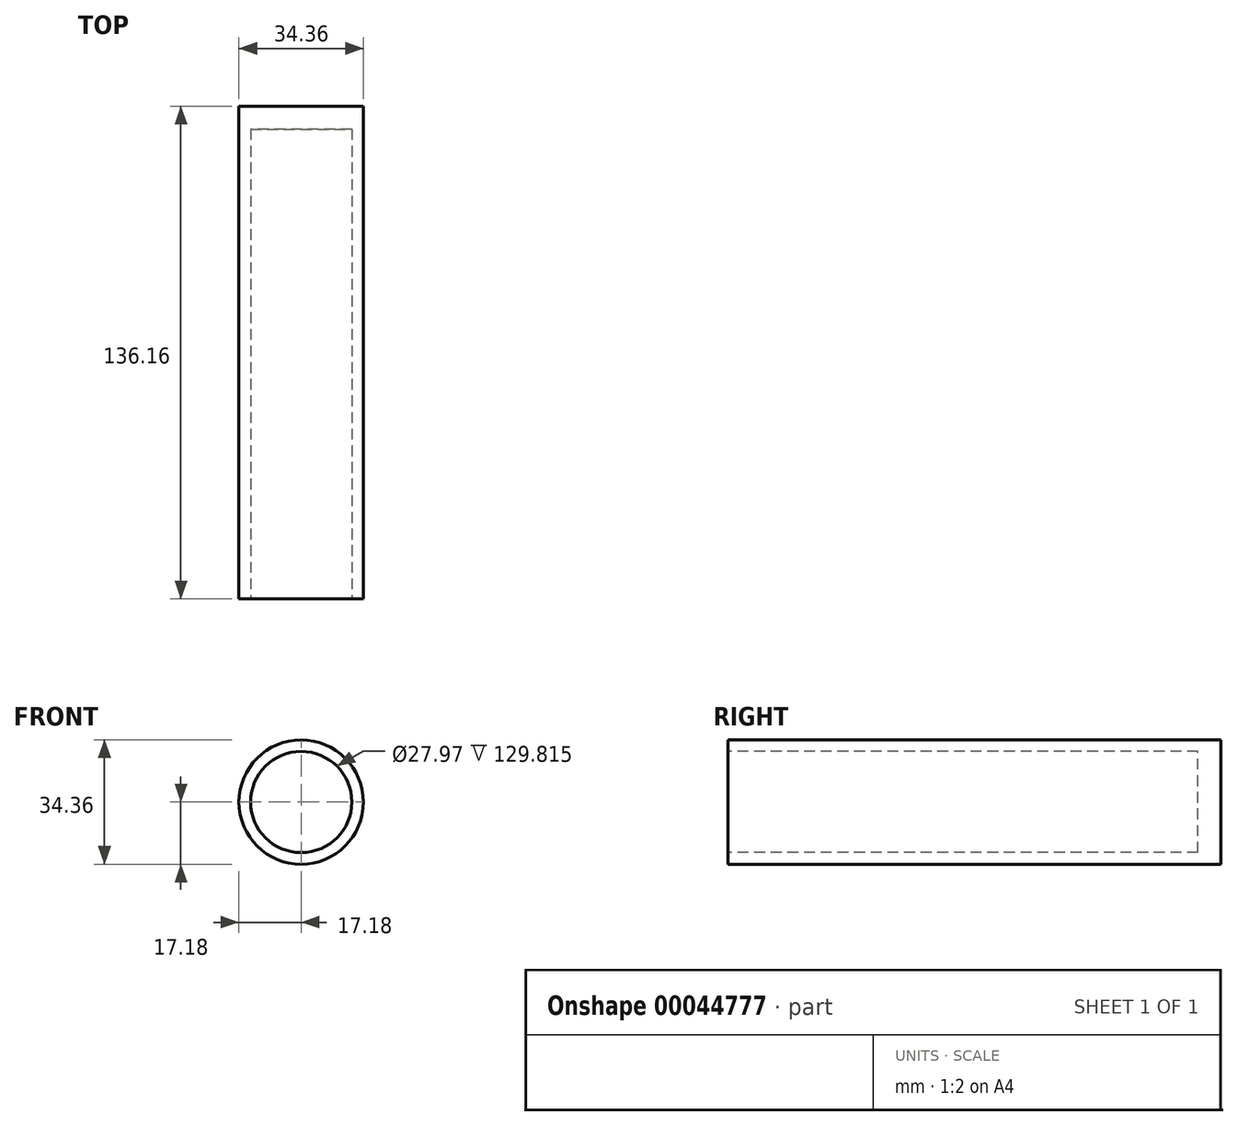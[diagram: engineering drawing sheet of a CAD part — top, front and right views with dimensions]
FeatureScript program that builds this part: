
annotation { "Feature Type Name" : "Feature", "Feature Type Description" : "" }
export const myFeature = defineFeature(function(context is Context, id is Id, definition is map)
    precondition{}
    {
        {
            var Q0;
            Q0=qCreatedBy(makeId("Front.planeOp"),FACE);
            var sketch = newSketch(context, id + "F0", { "sketchPlane" : qUnion([Q0])});
            skCircle(sketch, "E0", {"center": v(0, 0) * mm, "radius": 17.18 * mm});
            skSolve(sketch);
        }
        {
            var Q0;
            Q0=makeQuery(id+"F0.imprint","IMPRINT",FACE,{"disambiguationData":[TD([[makeQuery(id+"F0.imprint","IMPRINT",EDGE,{"derivedFrom":sQuery(id+"F0.wireOp",EDGE,"E0")}),1.0]])]});
            cPlane(context, id + "F1", {"entities" : qUnion([Q0]), "cplaneType" : CPlaneType.OFFSET, "offset" : 6.35 * mm, "width" : 152.4 * mm, "height" : 152.4 * mm});
        }
        {
            var Q0;
            Q0=makeQuery(id+"F0.imprint","IMPRINT",FACE,{"disambiguationData":[TD([[makeQuery(id+"F0.imprint","IMPRINT",EDGE,{"derivedFrom":sQuery(id+"F0.wireOp",EDGE,"E0")}),1.0]])]});
            extrude(context, id + "F2", {"entities" : qUnion([Q0]), "depth" : 136.16 * mm});
        }
        {
            var Q0;
            Q0=makeQuery(id+"F2.opExtrude","CAP_FACE",FACE,{"disambiguationData":[OSD([sQuery(id+"F0.wireOp",EDGE,"E0")])],"isStart":false});
            var sketch = newSketch(context, id + "F3", { "sketchPlane" : qUnion([Q0])});
            skCircle(sketch, "E1", {"center": v(0, 0) * mm, "radius": 13.99 * mm});
            skSolve(sketch);
        }
        {
            var Q0;
            Q0=makeQuery(id+"F3.imprint","IMPRINT",FACE,{"disambiguationData":[TD([[makeQuery(id+"F3.imprint","IMPRINT",EDGE,{"derivedFrom":sQuery(id+"F3.wireOp",EDGE,"E1")}),1.0]])]});
            var Q1;
            Q1=qCreatedBy(id+"F1.planeOp",FACE);
            extrude(context, id + "F4", {"entities" : qUnion([Q0]), "operationType" : NewBodyOperationType.REMOVE, "endBound" : BoundingType.UP_TO_SURFACE, "oppositeDirection" : true, "endBoundEntityFace" : qUnion([Q1]), "depth" : 25.4 * mm});
        }
    });
